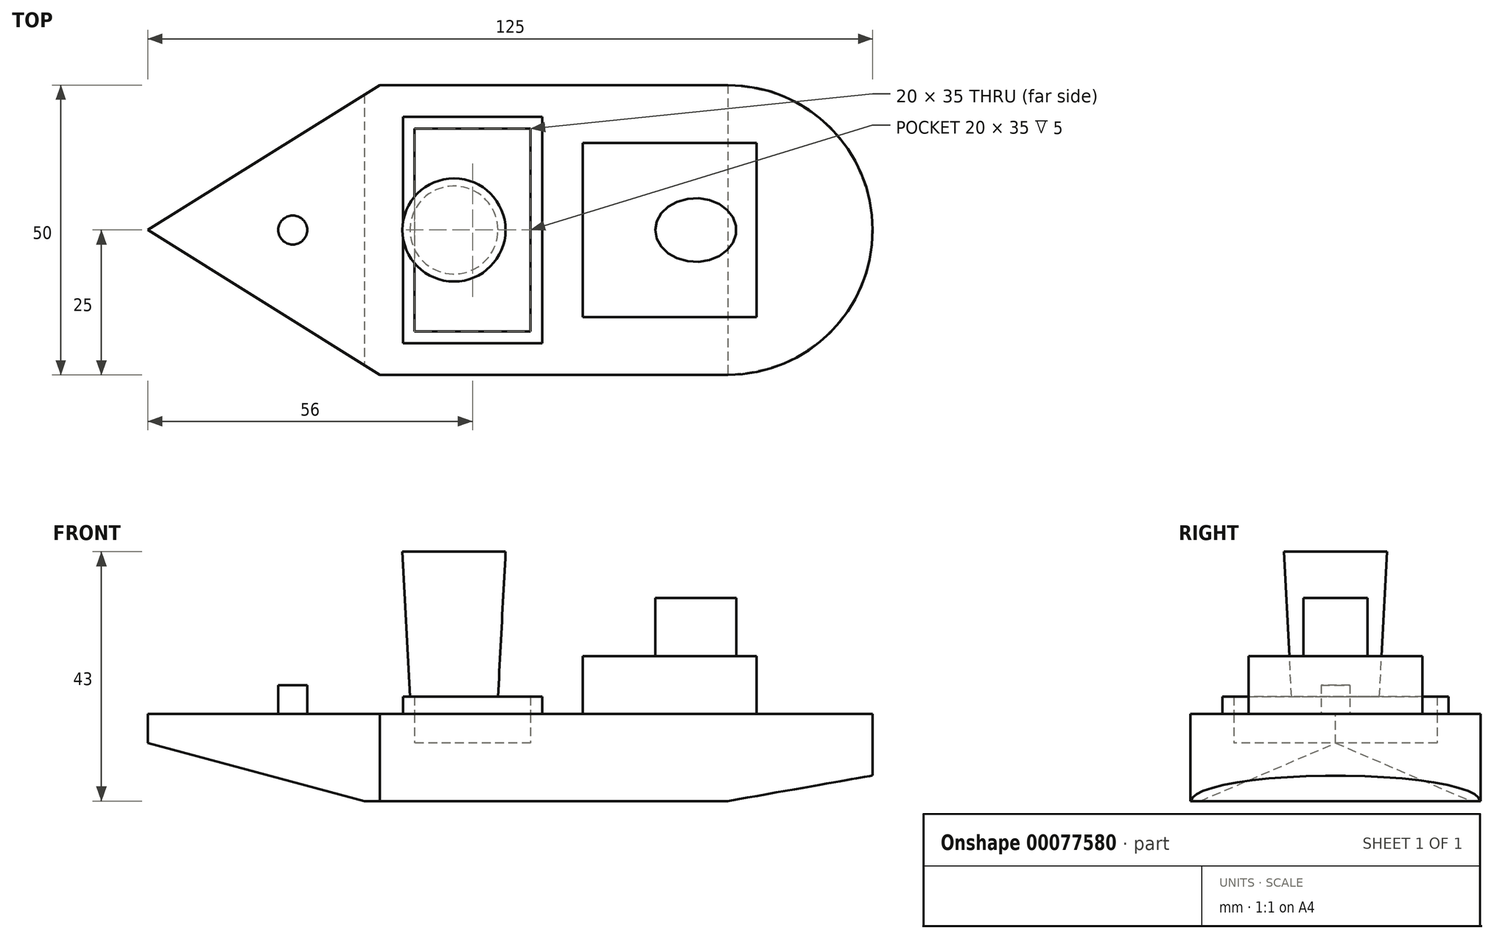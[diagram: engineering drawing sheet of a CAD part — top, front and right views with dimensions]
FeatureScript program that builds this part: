
annotation { "Feature Type Name" : "Feature", "Feature Type Description" : "" }
export const myFeature = defineFeature(function(context is Context, id is Id, definition is map)
    precondition{}
    {
        {
            var Q0;
            Q0=qCreatedBy(makeId("Front.planeOp"),FACE);
            var sketch = newSketch(context, id + "F0", { "sketchPlane" : qUnion([Q0])});
            skLineSegment(sketch, "E0.bottom", {"start": v(62.5, -7.5) * mm, "end": v(-62.5, -7.5) * mm});
            skLineSegment(sketch, "E0.top", {"start": v(62.5, 7.5) * mm, "end": v(-62.5, 7.5) * mm});
            skLineSegment(sketch, "E0.left", {"start": v(62.5, -7.5) * mm, "end": v(62.5, 7.5) * mm});
            skLineSegment(sketch, "E0.right", {"start": v(-62.5, -7.5) * mm, "end": v(-62.5, 7.5) * mm});
            skPoint(sketch, "E0.middle", {"position": v(0, 0) * mm});
            skSolve(sketch);
        }
        {
            var Q0;
            Q0=makeQuery(id+"F0.imprint","IMPRINT",FACE,{"disambiguationData":[TD([[makeQuery(id+"F0.imprint","IMPRINT",EDGE,{"derivedFrom":sQuery(id+"F0.wireOp",EDGE,"E0.bottom")}),-1.0]])]});
            extrude(context, id + "F1", {"entities" : qUnion([Q0]), "depth" : 50 * mm, "symmetric" : true});
        }
        {
            var Q0;
            Q0=makeQuery(id+"F1.opExtrude","CAP_EDGE",EDGE,{"disambiguationData":[OSD([sQuery(id+"F0.wireOp",EDGE,"E0.left")])],"isStart":false});
            var Q1;
            Q1=makeQuery(id+"F1.opExtrude","CAP_EDGE",EDGE,{"disambiguationData":[OSD([sQuery(id+"F0.wireOp",EDGE,"E0.left")])],"isStart":true});
            fillet(context, id + "F2", {"entities" : qUnion([Q0, Q1]), "radius" : 25 * mm, "tangentPropagation" : true, "allowEdgeOverflow" : false});
        }
        {
            var Q0;
            Q0=makeQuery(id+"F1.opExtrude","CAP_FACE",FACE,{"disambiguationData":[OSD([sQuery(id+"F0.wireOp",EDGE,"E0.bottom"),sQuery(id+"F0.wireOp",EDGE,"E0.top"),sQuery(id+"F0.wireOp",EDGE,"E0.left"),sQuery(id+"F0.wireOp",EDGE,"E0.right")])],"isStart":false});
            var sketch = newSketch(context, id + "F3", { "sketchPlane" : qUnion([Q0])});
            skLineSegment(sketch, "E1", {"start": v(-62.5, 2.5) * mm, "end": v(-25.18, -7.5) * mm});
            skSolve(sketch);
        }
        {
            var Q0;
            {var subQ0=sQuery(id+"F3.wireOp",EDGE,"E1");Q0=makeQuery(id+"F3.imprint","IMPRINT",FACE,{"disambiguationData":[TD([[makeQuery(id+"F3.imprint","IMPRINT",EDGE,{"derivedFrom":subQ0}),-1.0]])]});}
            extrude(context, id + "F4", {"entities" : qUnion([Q0]), "operationType" : NewBodyOperationType.REMOVE, "endBound" : BoundingType.THROUGH_ALL, "oppositeDirection" : true, "depth" : 25 * mm});
        }
        {
            var Q0;
            Q0=makeQuery(id+"F1.opExtrude","SWEPT_FACE",FACE,{"disambiguationData":[OSD([sQuery(id+"F0.wireOp",EDGE,"E0.top")])]});
            var sketch = newSketch(context, id + "F5", { "sketchPlane" : qUnion([Q0])});
            skLineSegment(sketch, "E2", {"start": v(-62.5, 0) * mm, "end": v(-22.5, -25) * mm});
            skLineSegment(sketch, "E3", {"start": v(-22.5, -25) * mm, "end": v(-22.5, 25) * mm});
            skLineSegment(sketch, "E4", {"start": v(-22.5, 25) * mm, "end": v(-62.5, 0) * mm});
            skSolve(sketch);
        }
        {
            var Q0;
            {var subQ0=sQuery(id+"F5.wireOp",EDGE,"E2");Q0=makeQuery(id+"F5.imprint","IMPRINT",FACE,{"disambiguationData":[TD([[makeQuery(id+"F5.imprint","IMPRINT",EDGE,{"derivedFrom":subQ0}),-1.0]])]});}
            var Q1;
            {var subQ0=sQuery(id+"F5.wireOp",EDGE,"E4");Q1=makeQuery(id+"F5.imprint","IMPRINT",FACE,{"disambiguationData":[TD([[makeQuery(id+"F5.imprint","IMPRINT",EDGE,{"derivedFrom":subQ0}),-1.0]])]});}
            extrude(context, id + "F6", {"entities" : qUnion([Q0, Q1]), "operationType" : NewBodyOperationType.REMOVE, "oppositeDirection" : true, "depth" : 25 * mm});
        }
        {
            var Q0;
            Q0=makeQuery(id+"F1.opExtrude","CAP_FACE",FACE,{"disambiguationData":[OSD([sQuery(id+"F0.wireOp",EDGE,"E0.bottom"),sQuery(id+"F0.wireOp",EDGE,"E0.top"),sQuery(id+"F0.wireOp",EDGE,"E0.left"),sQuery(id+"F0.wireOp",EDGE,"E0.right")])],"isStart":false});
            var sketch = newSketch(context, id + "F7", { "sketchPlane" : qUnion([Q0])});
            skLineSegment(sketch, "E5", {"start": v(37.5, -7.5) * mm, "end": v(96.81, 2.96) * mm});
            skLineSegment(sketch, "E6", {"start": v(96.81, 2.96) * mm, "end": v(96.81, -7.5) * mm});
            skLineSegment(sketch, "E7", {"start": v(96.81, -7.5) * mm, "end": v(37.5, -7.5) * mm});
            skSolve(sketch);
        }
        {
            var Q0;
            Q0=makeQuery(id+"F7.imprint","IMPRINT",FACE,{"disambiguationData":[TD([[makeQuery(id+"F7.imprint","IMPRINT",EDGE,{"derivedFrom":sQuery(id+"F7.wireOp",EDGE,"E5")}),-1.0]])]});
            extrude(context, id + "F8", {"entities" : qUnion([Q0]), "operationType" : NewBodyOperationType.REMOVE, "endBound" : BoundingType.THROUGH_ALL, "oppositeDirection" : true, "depth" : 25 * mm});
        }
        {
            var Q0;
            Q0=makeQuery(id+"F1.opExtrude","SWEPT_FACE",FACE,{"disambiguationData":[OSD([sQuery(id+"F0.wireOp",EDGE,"E0.top")])]});
            var sketch = newSketch(context, id + "F9", { "sketchPlane" : qUnion([Q0])});
            skLineSegment(sketch, "E8.bottom", {"start": v(12.5, -15) * mm, "end": v(42.5, -15) * mm});
            skLineSegment(sketch, "E8.top", {"start": v(12.5, 15) * mm, "end": v(42.5, 15) * mm});
            skLineSegment(sketch, "E8.left", {"start": v(12.5, -15) * mm, "end": v(12.5, 15) * mm});
            skLineSegment(sketch, "E8.right", {"start": v(42.5, -15) * mm, "end": v(42.5, 15) * mm});
            skSolve(sketch);
        }
        {
            var Q0;
            Q0=makeQuery(id+"F9.imprint","IMPRINT",FACE,{"disambiguationData":[TD([[makeQuery(id+"F9.imprint","IMPRINT",EDGE,{"derivedFrom":sQuery(id+"F9.wireOp",EDGE,"E8.bottom")}),1.0]])]});
            extrude(context, id + "F10", {"entities" : qUnion([Q0]), "depth" : 10 * mm});
        }
        {
            var Q0;
            Q0=qCreatedBy(makeId("Front.planeOp"),FACE);
            var sketch = newSketch(context, id + "F11", { "sketchPlane" : qUnion([Q0])});
            skLineSegment(sketch, "E9.bottom", {"start": v(3.5, 7.5) * mm, "end": v(-16.5, 7.5) * mm});
            skLineSegment(sketch, "E9.top", {"start": v(3.5, 2.5) * mm, "end": v(-16.5, 2.5) * mm});
            skLineSegment(sketch, "E9.left", {"start": v(3.5, 7.5) * mm, "end": v(3.5, 2.5) * mm});
            skLineSegment(sketch, "E9.right", {"start": v(-16.5, 7.5) * mm, "end": v(-16.5, 2.5) * mm});
            skSolve(sketch);
        }
        {
            var Q0;
            Q0 = qSketchRegion(id + "F11", true);
            extrude(context, id + "F12", {"entities" : qUnion([Q0]), "operationType" : NewBodyOperationType.REMOVE, "oppositeDirection" : true, "depth" : 35 * mm, "symmetric" : true});
        }
        {
            var Q0;
            Q0=makeQuery(id+"F10.opExtrude","CAP_FACE",FACE,{"disambiguationData":[OSD([sQuery(id+"F9.wireOp",EDGE,"E8.bottom"),sQuery(id+"F9.wireOp",EDGE,"E8.top"),sQuery(id+"F9.wireOp",EDGE,"E8.left"),sQuery(id+"F9.wireOp",EDGE,"E8.right")])],"isStart":false});
            var sketch = newSketch(context, id + "F13", { "sketchPlane" : qUnion([Q0])});
            skEllipse(sketch, "E10", {"center": v(32, 0) * mm, "majorRadius": 7 * mm, "minorRadius": 5.5 * mm, "majorAxis": v(-1, 0)});
            skSolve(sketch);
        }
        {
            var Q0;
            Q0=makeQuery(id+"F13.imprint","IMPRINT",FACE,{"disambiguationData":[TD([[makeQuery(id+"F13.imprint","IMPRINT",EDGE,{"derivedFrom":sQuery(id+"F13.wireOp",EDGE,"E10")}),1.0]])]});
            extrude(context, id + "F14", {"entities" : qUnion([Q0]), "depth" : 10 * mm});
        }
        {
            var Q0;
            Q0=makeQuery(id+"F1.opExtrude","SWEPT_FACE",FACE,{"disambiguationData":[OSD([sQuery(id+"F0.wireOp",EDGE,"E0.top")])]});
            var sketch = newSketch(context, id + "F15", { "sketchPlane" : qUnion([Q0])});
            skCircle(sketch, "E11", {"center": v(-37.5, 0) * mm, "radius": 2.5 * mm});
            skSolve(sketch);
        }
        {
            var Q0;
            Q0=makeQuery(id+"F15.imprint","IMPRINT",FACE,{"disambiguationData":[TD([[makeQuery(id+"F15.imprint","IMPRINT",EDGE,{"derivedFrom":sQuery(id+"F15.wireOp",EDGE,"E11")}),1.0]])]});
            extrude(context, id + "F16", {"entities" : qUnion([Q0]), "depth" : 5 * mm});
        }
        {
            var Q0;
            Q0=makeQuery(id+"F1.opExtrude","SWEPT_FACE",FACE,{"disambiguationData":[OSD([sQuery(id+"F0.wireOp",EDGE,"E0.top")])]});
            extrude(context, id + "F21", {"entities" : qUnion([Q0]), "depth" : 25 * mm});
        }
        {
            var Q0;
            Q0=makeQuery(id+"F21.opExtrude","SWEPT_BODY",BODY,{"disambiguationData":[OSD([sQuery(id+"F0.wireOp",EDGE,"E0.top")])]});
            deleteBodies(context, id + "F17", {"entities" : qUnion([Q0])});
        }
        {
            var Q0;
            Q0=makeQuery(id+"F1.opExtrude","SWEPT_FACE",FACE,{"disambiguationData":[OSD([sQuery(id+"F0.wireOp",EDGE,"E0.top")])]});
            var sketch = newSketch(context, id + "F18", { "sketchPlane" : qUnion([Q0])});
            skLineSegment(sketch, "E12.bottom", {"start": v(-18.5, -19.5) * mm, "end": v(5.5, -19.5) * mm});
            skLineSegment(sketch, "E12.top", {"start": v(-18.5, 19.5) * mm, "end": v(5.5, 19.5) * mm});
            skLineSegment(sketch, "E12.left", {"start": v(-18.5, -19.5) * mm, "end": v(-18.5, 19.5) * mm});
            skLineSegment(sketch, "E12.right", {"start": v(5.5, -19.5) * mm, "end": v(5.5, 19.5) * mm});
            skSolve(sketch);
        }
        {
            var Q0;
            Q0=makeQuery(id+"F18.imprint","IMPRINT",FACE,{"disambiguationData":[TD([[makeQuery(id+"F18.imprint","IMPRINT",EDGE,{"derivedFrom":sQuery(id+"F18.wireOp",EDGE,"E12.bottom")}),1.0]])]});
            var Q1;
            {var subQ0=sQuery(id+"F11.wireOp",EDGE,"E9.bottom");Q1=makeQuery(id+"F18.imprint","IMPRINT",FACE,{"disambiguationData":[TD([[makeQuery(id+"F18.imprint","IMPRINT",EDGE,{"derivedFrom":makeQuery(id+"F12.boolean.opBoolean","COPY",EDGE,{"derivedFrom":makeQuery(id+"F12.opExtrude","CAP_EDGE",EDGE,{"disambiguationData":[OSD([subQ0])],"isStart":true})})}),-1.0]])]});}
            extrude(context, id + "F19", {"entities" : qUnion([Q0, Q1]), "depth" : 3 * mm});
        }
        {
            var Q0;
            Q0=makeQuery(id+"F19.opExtrude","CAP_FACE",FACE,{"disambiguationData":[OSD([sQuery(id+"F18.wireOp",EDGE,"E12.bottom"),sQuery(id+"F18.wireOp",EDGE,"E12.top"),sQuery(id+"F18.wireOp",EDGE,"E12.left"),sQuery(id+"F18.wireOp",EDGE,"E12.right")])],"isStart":false});
            var sketch = newSketch(context, id + "F20", { "sketchPlane" : qUnion([Q0])});
            skCircle(sketch, "E13", {"center": v(-9.7, 0) * mm, "radius": 7.58 * mm});
            skSolve(sketch);
        }
        {
            var Q0;
            Q0=makeQuery(id+"F20.imprint","IMPRINT",FACE,{"disambiguationData":[TD([[makeQuery(id+"F20.imprint","IMPRINT",EDGE,{"derivedFrom":sQuery(id+"F20.wireOp",EDGE,"E13")}),1.0]])]});
            extrude(context, id + "F22", {"entities" : qUnion([Q0]), "operationType" : NewBodyOperationType.ADD, "depth" : 25 * mm, "hasDraft" : true, "draftAngle" : 3 * degree});
        }
    });
